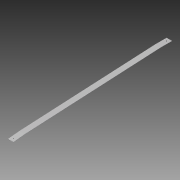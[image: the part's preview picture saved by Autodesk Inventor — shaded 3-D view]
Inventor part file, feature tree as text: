
AUTODESK INVENTOR PART (.ipt)
format: ipt  version: 2014 (Build 180170000, 170)  size: 168,960 bytes
history: native  units: in
note: dims shown in document units (in); Inventor stores cm internally (conversion verified against a paired STEP export)
features: sketch x6, hole x3, sheet_metal_op x2, extrude x1, other x1
ambient origin geometry x8: Origin, YZ Plane, XZ Plane, XY Plane, X Axis, Y Axis, Z Axis, Center Point
bodies: Solid1 (feature_tree)
feature tree (13):
  extrude  "Extrusion1"  Depth=0.0394in
  hole  "Hole1"  [1 undecoded]
  hole  "Hole2"  [1 undecoded]
  sheet_metal_op  "Fold2"
  sheet_metal_op  "Fold3"
  hole  "Hole3"  [1 undecoded]
  sketch  "Sketch1"  dims[d0=1.5in d1=0.0394in]
  sketch  "Sketch2"  dims[d2=43.7008in d3=0.0in d4=0.7874in]
  sketch  "Sketch3"  dims[d5=0.252in d6=0.75in d7=0.375in d8=0.25in d9=0.5635in d10=1.0in d11=0.8108in d12=0.7874in]
  sketch  "Sketch6"  dims[d13=0.252in d14=0.75in d15=0.375in d16=0.25in d17=0.5635in d18=1.0in d19=0.8108in d29=2.3622in]
  sketch  "Sketch7"  dims[d30=0.0in]
  sketch  "Sketch8"  dims[d31=0.0394in d32=0.0197in d33=0.0787in d34=0.0394in d35=0.0206in d36=0.0394in d37=0.0in d38=0.0394in d39=0.0197in d40=0.0787in d41=0.0394in d42=0.0206in d43=0.0394in d44=2.3622in d45=3.937in d46=0.0394in d47=0.2362in d48=0.1575in d49=0.0787in d50=90.0deg d51=0.0394in d52=0.8108in]
  other  "Definition1"
note: 3 required parameter values undecoded (feature->parameter linkage not recoverable at this tier; creation-order binding heuristic only, values carry confidence <= 0.55)
